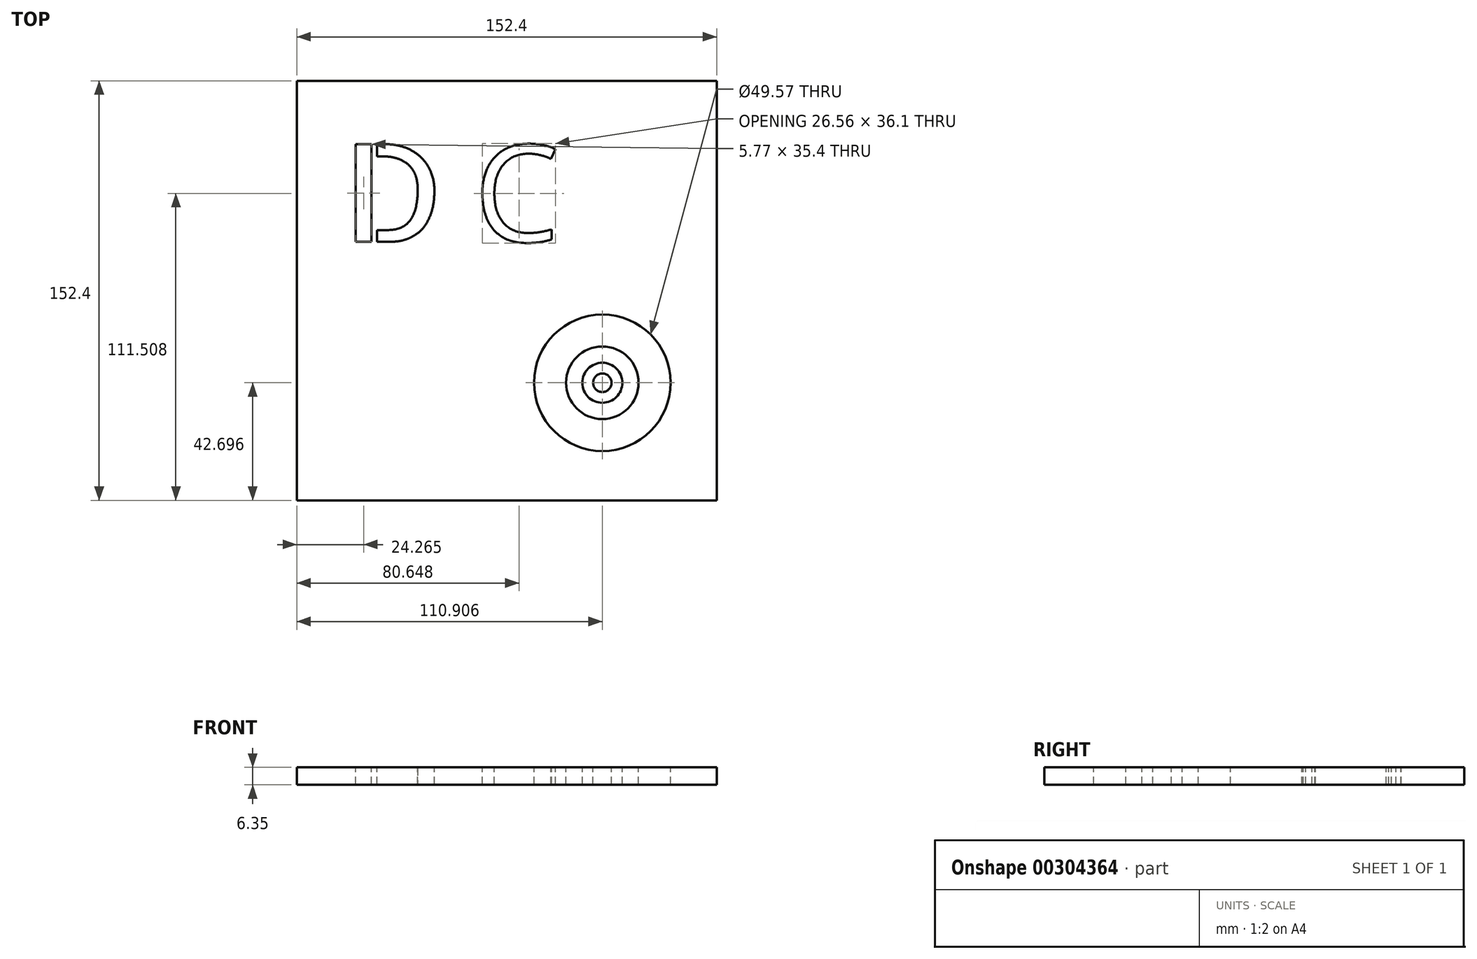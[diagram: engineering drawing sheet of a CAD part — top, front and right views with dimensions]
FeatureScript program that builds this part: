
annotation { "Feature Type Name" : "Feature", "Feature Type Description" : "" }
export const myFeature = defineFeature(function(context is Context, id is Id, definition is map)
    precondition{}
    {
        {
            var Q0;
            Q0=qCreatedBy(makeId("Top.planeOp"),FACE);
            var sketch = newSketch(context, id + "F0", { "sketchPlane" : qUnion([Q0])});
            skLineSegment(sketch, "E0.bottom", {"start": v(-76.2, -76.2) * mm, "end": v(76.2, -76.2) * mm});
            skLineSegment(sketch, "E0.top", {"start": v(-76.2, 76.2) * mm, "end": v(76.2, 76.2) * mm});
            skLineSegment(sketch, "E0.left", {"start": v(-76.2, -76.2) * mm, "end": v(-76.2, 76.2) * mm});
            skLineSegment(sketch, "E0.right", {"start": v(76.2, -76.2) * mm, "end": v(76.2, 76.2) * mm});
            skPoint(sketch, "E0.middle", {"position": v(0, 0) * mm});
            skText(sketch, "E1", { "text": "D", "fontName": "AllertaStencil-Regular.ttf"});
            skText(sketch, "E2", { "text": "C", "fontName": "OpenSans-Regular.ttf"});
            skCircle(sketch, "E3", {"center": v(34.7, -33.5) * mm, "radius": 24.78 * mm});
            skCircle(sketch, "E4", {"center": v(34.7, -33.5) * mm, "radius": 13.17 * mm});
            skCircle(sketch, "E5", {"center": v(34.7, -33.5) * mm, "radius": 7.27 * mm});
            skCircle(sketch, "E6", {"center": v(34.7, -33.5) * mm, "radius": 3.36 * mm});
            const initialGuessF0  = {"E1": [-0.05943, 0.01774, 1, 0, 0.03542], "E2": [-0.01184, 0.01774, 1, 0, 0.03542]};
            skSetInitialGuess(sketch, initialGuessF0);
            skSolve(sketch);
        }
        {
            var Q0;
            Q0 = qSketchRegion(id + "F0", true);
            var Q1;
            Q1=makeQuery(id+"F0.imprint","IMPRINT",FACE,{"disambiguationData":[TD([[makeQuery(id+"F0.imprint","IMPRINT",EDGE,{"derivedFrom":sQuery(id+"F0.wireOp",EDGE,"E4")}),1.0]])]});
            var Q2;
            Q2=makeQuery(id+"F0.imprint","IMPRINT",FACE,{"disambiguationData":[TD([[makeQuery(id+"F0.imprint","IMPRINT",EDGE,{"derivedFrom":sQuery(id+"F0.wireOp",EDGE,"E6")}),1.0]])]});
            extrude(context, id + "F1", {"entities" : qUnion([Q0, Q1, Q2]), "oppositeDirection" : true, "depth" : 6.35 * mm});
        }
    });
